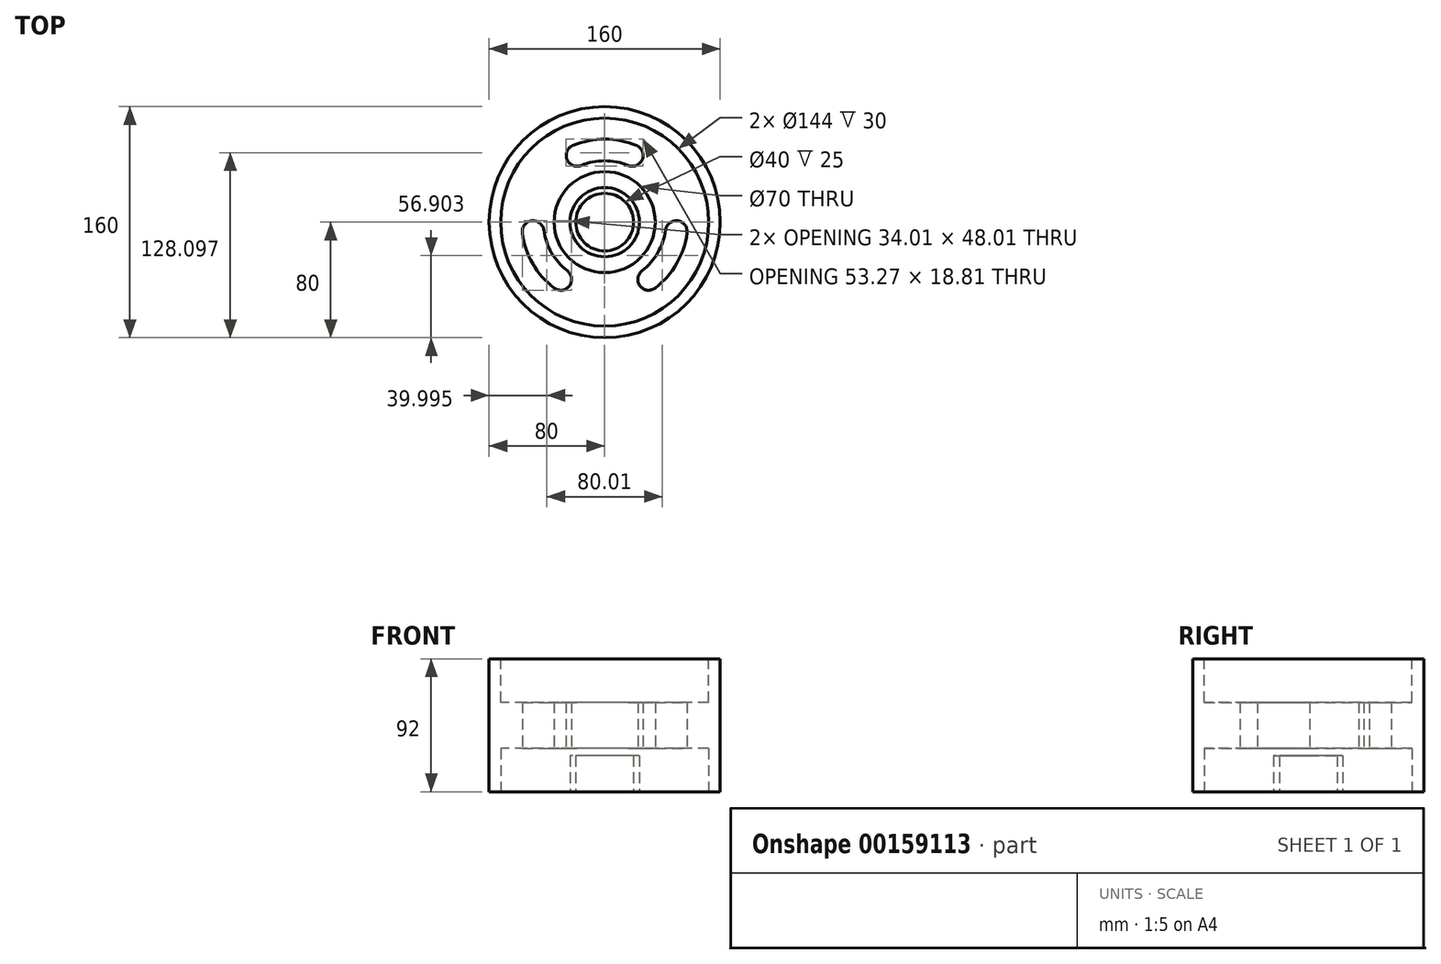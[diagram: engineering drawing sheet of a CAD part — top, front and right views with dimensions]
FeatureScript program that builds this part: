
annotation { "Feature Type Name" : "Feature", "Feature Type Description" : "" }
export const myFeature = defineFeature(function(context is Context, id is Id, definition is map)
    precondition{}
    {
        {
            var Q0;
            Q0=qCreatedBy(makeId("Top.planeOp"),FACE);
            var sketch = newSketch(context, id + "F0", { "sketchPlane" : qUnion([Q0])});
            skCircle(sketch, "E0", {"center": v(0, 0) * mm, "radius": 20 * mm});
            skCircle(sketch, "E1", {"center": v(0, 0) * mm, "radius": 24 * mm});
            skCircle(sketch, "E2", {"center": v(0, 0) * mm, "radius": 35 * mm});
            skPoint(sketch, "E3", {"position": v(-19.13, 46.2) * mm});
            skPoint(sketch, "E4", {"position": v(19.13, 46.2) * mm});
            skCircle(sketch, "E5", {"center": v(0, 0) * mm, "radius": 50 * mm, "construction": true});
            skLineSegment(sketch, "E6", {"start": v(0, 0) * mm, "end": v(0, 50) * mm, "construction": true});
            skLineSegment(sketch, "E7", {"start": v(0, 0) * mm, "end": v(-19.13, 46.2) * mm, "construction": true});
            skLineSegment(sketch, "E8", {"start": v(19.13, 46.2) * mm, "end": v(0, 0) * mm, "construction": true});
            skPoint(sketch, "E9", {"position": v(0, 58.96) * mm});
            skLineSegment(sketch, "E10", {"start": v(0, 0) * mm, "end": v(-28.08, 67.79) * mm, "construction": true});
            skLineSegment(sketch, "E11", {"start": v(0, 0) * mm, "end": v(25.96, 62.67) * mm, "construction": true});
            skCircle(sketch, "E12", {"center": v(-19.13, 46.2) * mm, "radius": 7.5 * mm});
            skArc(sketch, "E13", {"start": v(16.26, 39.26) * mm, "mid": v(26.06, 43.32) * mm, "end": v(22, 53.12) * mm});
            skArc(sketch, "E14", {"start": v(16.26, 39.26) * mm, "mid": v(0, 42.5) * mm, "end": v(-16.26, 39.26) * mm});
            skArc(sketch, "E15", {"start": v(22, 53.12) * mm, "mid": v(0, 57.5) * mm, "end": v(-22, 53.12) * mm});
            skPoint(sketch, "E16.1.0", {"position": v(-49.57, -6.53) * mm});
            skCircle(sketch, "E16.1.2", {"center": v(-30.44, -39.67) * mm, "radius": 7.5 * mm});
            skArc(sketch, "E16.1.3", {"start": v(-42.14, -5.55) * mm, "mid": v(-50.55, 0.9) * mm, "end": v(-57, -7.5) * mm});
            skArc(sketch, "E16.1.4", {"start": v(-42.14, -5.55) * mm, "mid": v(-36.8, -21.25) * mm, "end": v(-25.87, -33.72) * mm});
            skArc(sketch, "E16.1.5", {"start": v(-57, -7.5) * mm, "mid": v(-49.8, -28.75) * mm, "end": v(-35, -45.62) * mm});
            skPoint(sketch, "E16.2.0", {"position": v(30.44, -39.67) * mm});
            skCircle(sketch, "E16.2.2", {"center": v(49.57, -6.53) * mm, "radius": 7.5 * mm});
            skArc(sketch, "E16.2.3", {"start": v(25.87, -33.72) * mm, "mid": v(24.49, -44.23) * mm, "end": v(35, -45.62) * mm});
            skArc(sketch, "E16.2.4", {"start": v(25.87, -33.72) * mm, "mid": v(36.8, -21.25) * mm, "end": v(42.14, -5.55) * mm});
            skArc(sketch, "E16.2.5", {"start": v(35, -45.62) * mm, "mid": v(49.8, -28.75) * mm, "end": v(57, -7.5) * mm});
            skLineSegment(sketch, "E17", {"start": v(-49.57, -6.53) * mm, "end": v(0, 0) * mm, "construction": true});
            skLineSegment(sketch, "E18", {"start": v(-30.44, -39.67) * mm, "end": v(0, 0) * mm, "construction": true});
            skLineSegment(sketch, "E19", {"start": v(51.61, -6.53) * mm, "end": v(0, 0) * mm, "construction": true});
            skLineSegment(sketch, "E20", {"start": v(30.44, -39.67) * mm, "end": v(0, 0) * mm, "construction": true});
            skCircle(sketch, "E21", {"center": v(0, 0) * mm, "radius": 80 * mm});
            skCircle(sketch, "E22", {"center": v(0, 0) * mm, "radius": 72 * mm});
            skSolve(sketch);
        }
        {
            var Q0;
            Q0 = qSketchRegion(id + "F0", true);
            extrude(context, id + "F1", {"entities" : qUnion([Q0]), "depth" : 92 * mm});
        }
        {
            var Q0;
            Q0 = qSketchRegion(id + "F0", true);
            var Q1;
            Q1=makeQuery(id+"F0.imprint","IMPRINT",FACE,{"disambiguationData":[TD([[makeQuery(id+"F0.imprint","IMPRINT",EDGE,{"derivedFrom":sQuery(id+"F0.wireOp",EDGE,"E2")}),-1.0]])]});
            extrude(context, id + "F2", {"entities" : qUnion([Q0, Q1]), "operationType" : NewBodyOperationType.ADD, "depth" : 92 * mm});
        }
        {
            var Q0;
            Q0=makeQuery(id+"F0.imprint","IMPRINT",FACE,{"disambiguationData":[TD([[makeQuery(id+"F0.imprint","IMPRINT",EDGE,{"derivedFrom":sQuery(id+"F0.wireOp",EDGE,"E2")}),-1.0]])]});
            var Q1;
            Q1=sQuery(id+"F0.wireOp",EDGE,"E22");
            extrude(context, id + "F3", {"entities" : qUnion([Q0]), "operationType" : NewBodyOperationType.REMOVE, "surfaceEntities" : qUnion([Q1]), "depth" : 30 * mm});
        }
        {
            var Q0;
            Q0=makeQuery(id+"F0.imprint","IMPRINT",FACE,{"disambiguationData":[TD([[makeQuery(id+"F0.imprint","IMPRINT",EDGE,{"derivedFrom":sQuery(id+"F0.wireOp",EDGE,"E2")}),-1.0]])]});
            var sketch = newSketch(context, id + "F4", { "sketchPlane" : qUnion([Q0])});
            skCircle(sketch, "E23.0.0", {"center": v(0, 0) * mm, "radius": 72 * mm});
            skArc(sketch, "E24.0", {"start": v(-42.14, -5.55) * mm, "mid": v(-50.55, 0.9) * mm, "end": v(-57, -7.5) * mm});
            skArc(sketch, "E25.0", {"start": v(-57, -7.5) * mm, "mid": v(-49.8, -28.75) * mm, "end": v(-35, -45.62) * mm});
            skArc(sketch, "E26.0", {"start": v(-42.14, -5.55) * mm, "mid": v(-36.8, -21.25) * mm, "end": v(-25.87, -33.72) * mm});
            skCircle(sketch, "E27.0", {"center": v(-30.44, -39.67) * mm, "radius": 7.5 * mm});
            skArc(sketch, "E28.0", {"start": v(25.87, -33.72) * mm, "mid": v(24.49, -44.23) * mm, "end": v(35, -45.62) * mm});
            skArc(sketch, "E29.0", {"start": v(25.87, -33.72) * mm, "mid": v(36.8, -21.25) * mm, "end": v(42.14, -5.55) * mm});
            skCircle(sketch, "E30.0", {"center": v(49.57, -6.53) * mm, "radius": 7.5 * mm});
            skArc(sketch, "E31.0", {"start": v(35, -45.62) * mm, "mid": v(49.8, -28.75) * mm, "end": v(57, -7.5) * mm});
            skArc(sketch, "E32.0", {"start": v(16.26, 39.26) * mm, "mid": v(26.06, 43.32) * mm, "end": v(22, 53.12) * mm});
            skCircle(sketch, "E33.0", {"center": v(0, 0) * mm, "radius": 35 * mm});
            skArc(sketch, "E34.0", {"start": v(16.26, 39.26) * mm, "mid": v(0, 42.5) * mm, "end": v(-16.26, 39.26) * mm});
            skCircle(sketch, "E35.0", {"center": v(-19.13, 46.2) * mm, "radius": 7.5 * mm});
            skArc(sketch, "E36.0", {"start": v(22, 53.12) * mm, "mid": v(0, 57.5) * mm, "end": v(-22, 53.12) * mm});
            skSolve(sketch);
        }
        {
            var Q0;
            Q0 = qSketchRegion(id + "F4", true);
            extrude(context, id + "F5", {"entities" : qUnion([Q0]), "operationType" : NewBodyOperationType.REMOVE, "depth" : 30 * mm});
        }
        {
            var Q0;
            {var subQ0=sQuery(id+"F0.wireOp",EDGE,"E21");Q0=makeQuery(id+"F2.boolean.opBoolean","MERGE",FACE,{"derivedFrom":[makeQuery(id+"F1.opExtrude","CAP_FACE",FACE,{"disambiguationData":[OSD([subQ0,sQuery(id+"F0.wireOp",EDGE,"E22")])],"isStart":false}),makeQuery(id+"F2.opExtrude","CAP_FACE",FACE,{"disambiguationData":[OSD([sQuery(id+"F0.wireOp",EDGE,"E2"),sQuery(id+"F0.wireOp",EDGE,"E12"),sQuery(id+"F0.wireOp",EDGE,"E13"),sQuery(id+"F0.wireOp",EDGE,"E14"),sQuery(id+"F0.wireOp",EDGE,"E15"),sQuery(id+"F0.wireOp",EDGE,"E16.1.2"),sQuery(id+"F0.wireOp",EDGE,"E16.1.3"),sQuery(id+"F0.wireOp",EDGE,"E16.1.4"),sQuery(id+"F0.wireOp",EDGE,"E16.1.5"),sQuery(id+"F0.wireOp",EDGE,"E16.2.2"),sQuery(id+"F0.wireOp",EDGE,"E16.2.3"),sQuery(id+"F0.wireOp",EDGE,"E16.2.4"),sQuery(id+"F0.wireOp",EDGE,"E16.2.5"),subQ0])],"isStart":false})]});}
            var sketch = newSketch(context, id + "F6", { "sketchPlane" : qUnion([Q0])});
            skCircle(sketch, "E37.0", {"center": v(0, 0) * mm, "radius": 72 * mm});
            skArc(sketch, "E38.0", {"start": v(-42.14, -5.55) * mm, "mid": v(-50.55, 0.9) * mm, "end": v(-57, -7.5) * mm});
            skArc(sketch, "E39.0", {"start": v(-42.14, -5.55) * mm, "mid": v(-36.8, -21.25) * mm, "end": v(-25.87, -33.72) * mm});
            skArc(sketch, "E40.0", {"start": v(-57, -7.5) * mm, "mid": v(-49.8, -28.75) * mm, "end": v(-35, -45.62) * mm});
            skCircle(sketch, "E41.0", {"center": v(-30.44, -39.67) * mm, "radius": 7.5 * mm});
            skArc(sketch, "E41.1", {"start": v(25.87, -33.72) * mm, "mid": v(24.49, -44.23) * mm, "end": v(35, -45.62) * mm});
            skCircle(sketch, "E41.2", {"center": v(49.57, -6.53) * mm, "radius": 7.5 * mm});
            skArc(sketch, "E41.3", {"start": v(35, -45.62) * mm, "mid": v(49.8, -28.75) * mm, "end": v(57, -7.5) * mm});
            skArc(sketch, "E41.4", {"start": v(25.87, -33.72) * mm, "mid": v(36.8, -21.25) * mm, "end": v(42.14, -5.55) * mm});
            skArc(sketch, "E42.0", {"start": v(22, 53.12) * mm, "mid": v(0, 57.5) * mm, "end": v(-22, 53.12) * mm});
            skCircle(sketch, "E43.0", {"center": v(-19.13, 46.2) * mm, "radius": 7.5 * mm});
            skArc(sketch, "E44.0", {"start": v(16.26, 39.26) * mm, "mid": v(0, 42.5) * mm, "end": v(-16.26, 39.26) * mm});
            skArc(sketch, "E45.0", {"start": v(16.26, 39.26) * mm, "mid": v(26.06, 43.32) * mm, "end": v(22, 53.12) * mm});
            skCircle(sketch, "E46.0", {"center": v(0, 0) * mm, "radius": 35 * mm});
            skSolve(sketch);
        }
        {
            var Q0;
            Q0 = qSketchRegion(id + "F6", true);
            extrude(context, id + "F7", {"entities" : qUnion([Q0]), "operationType" : NewBodyOperationType.REMOVE, "oppositeDirection" : true, "depth" : 25 * mm});
        }
        {
            var Q0;
            Q0 = qSketchRegion(id + "F6", true);
            extrude(context, id + "F8", {"entities" : qUnion([Q0]), "operationType" : NewBodyOperationType.REMOVE, "oppositeDirection" : true, "depth" : 30 * mm});
        }
        {
            var Q0;
            Q0=makeQuery(id+"F0.imprint","IMPRINT",FACE,{"disambiguationData":[TD([[makeQuery(id+"F0.imprint","IMPRINT",EDGE,{"derivedFrom":sQuery(id+"F0.wireOp",EDGE,"E0")}),-1.0]])]});
            var sketch = newSketch(context, id + "F9", { "sketchPlane" : qUnion([Q0])});
            skCircle(sketch, "E47.0", {"center": v(0, 0) * mm, "radius": 20 * mm});
            skCircle(sketch, "E48.0", {"center": v(0, 0) * mm, "radius": 24 * mm});
            skSolve(sketch);
        }
        {
            var Q0;
            Q0 = qSketchRegion(id + "F9", true);
            extrude(context, id + "F10", {"entities" : qUnion([Q0]), "depth" : 25 * mm});
        }
    });
